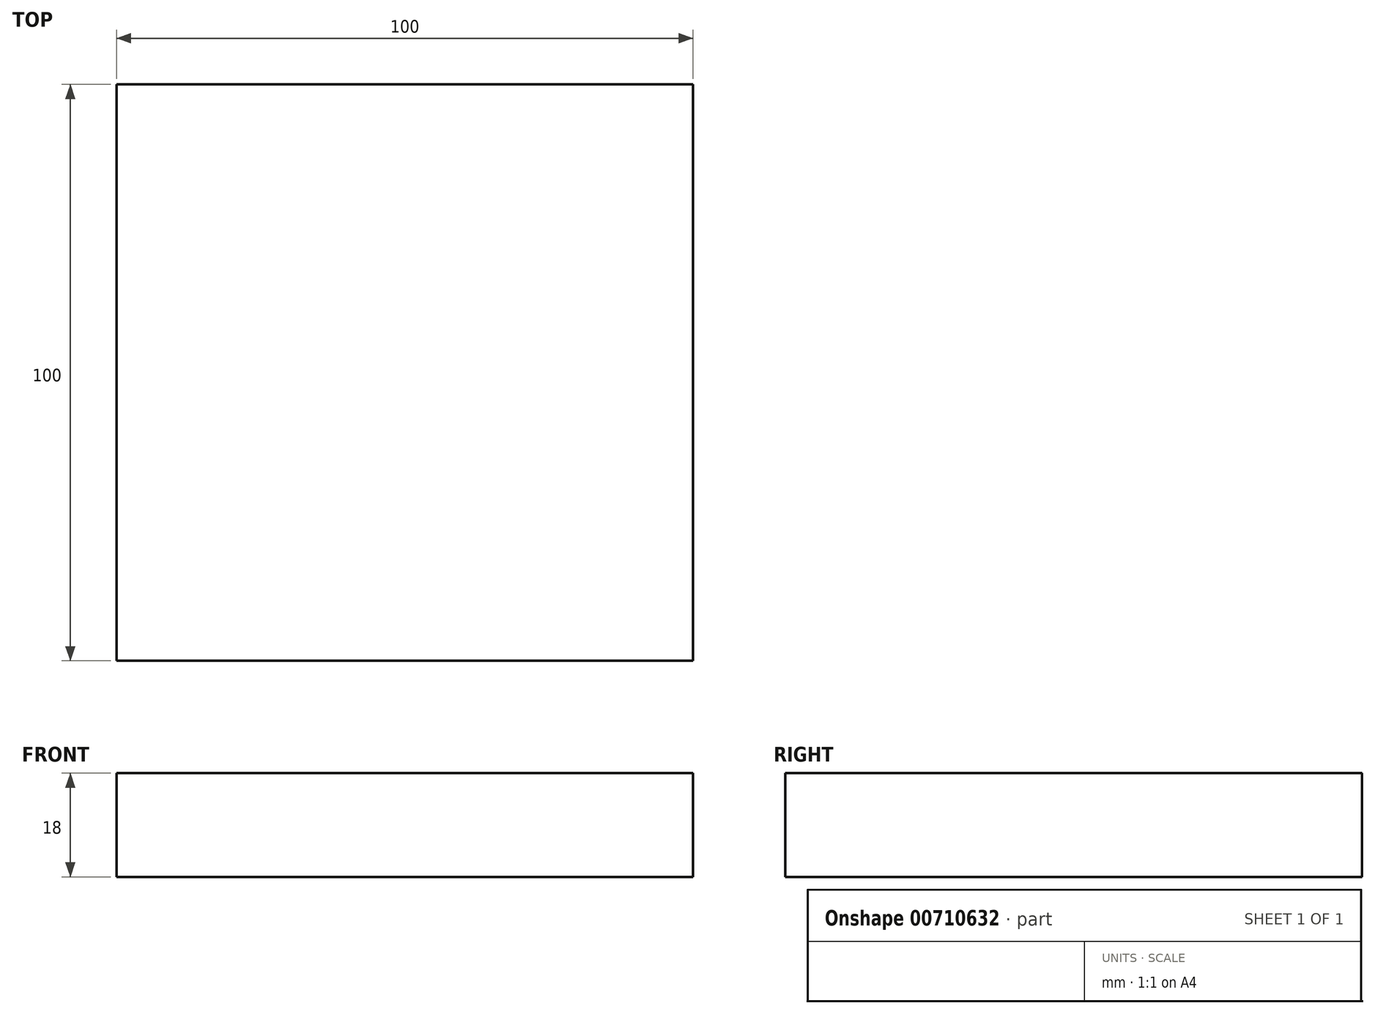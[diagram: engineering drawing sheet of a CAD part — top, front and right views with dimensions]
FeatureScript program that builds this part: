
annotation { "Feature Type Name" : "Feature", "Feature Type Description" : "" }
export const myFeature = defineFeature(function(context is Context, id is Id, definition is map)
    precondition{}
    {
        {
            var Q0;
            Q0=qCreatedBy(makeId("Top.planeOp"),FACE);
            var sketch = newSketch(context, id + "F0", { "sketchPlane" : qUnion([Q0])});
            skLineSegment(sketch, "E0.bottom", {"start": v(0, 0) * mm, "end": v(100, 0) * mm});
            skLineSegment(sketch, "E0.top", {"start": v(0, 100) * mm, "end": v(100, 100) * mm});
            skLineSegment(sketch, "E0.left", {"start": v(0, 0) * mm, "end": v(0, 100) * mm});
            skLineSegment(sketch, "E0.right", {"start": v(100, 0) * mm, "end": v(100, 100) * mm});
            skSolve(sketch);
        }
        {
            var Q0;
            Q0=makeQuery(id+"F0.imprint","IMPRINT",FACE,{"disambiguationData":[TD([[makeQuery(id+"F0.imprint","IMPRINT",EDGE,{"derivedFrom":sQuery(id+"F0.wireOp",EDGE,"E0.bottom")}),1.0]])]});
            extrude(context, id + "F1", {"entities" : qUnion([Q0]), "depth" : 18 * mm, "offsetDistance" : 25 * mm});
        }
    });
